# Revit family: ledtrunk_mod_l15-35w-4000-df-dali-em3-dz_549004010500
name_source: partatom
category: Leuchten
revit_build: Autodesk Revit 2016 (Build: 20190508_0715(x64)
units: mm (PartAtom-declared; Revit-internal decimal feet)

## family parameters
Basisbauteil = Fläche
Beim Laden mit Abzugskörper schneiden = Nein
Bemaßung runder Anschluss = Durchmesser verwenden
Gemeinsam genutzt = Nein
Lichtquelle = Nein
Raumberechnungspunkt = Nein
Teiletyp = Normal

## types (1)
- LEDTrunk Mod L15-35W-4000-DF-DALI-EM3-DZ (1 x LED, 5250 lm, 4000)
    Approval mark = CE, ENEC
    Beschreibung = Professional LED light line solution. Simple installation with snap-in mounting of LED modules and trunks. Integration of 3C Spots possible with 3C Track Module accessory.
    CIE Flux Codes = 41 71 90 89 99
    Color Rendering = 80
    Color Temperature = 4000
    Control Gear = Electronic ballast
    Frequency = 60 Hz
    Height = 66 mm
    Hersteller = OPPLE
    Lamp Light Flux = 5250 lm
    Lamp count = 1
    Lampe = 1 x LED
    Length = 1498 mm
    Luminous efficacy = 150 lm/W
    ModVariant = Nein
    Modell = 549004010500
    Mounting Place = Ceiling, Pole
    Mounting Type = Surface mounted, Pendant
    Number of Poles = 1
    OnlyDefault = Ja
    Power Factor = 1
    Product Name = LEDTrunk Mod L15-35W-4000-DF-DALI-EM3-DZ
    Product group = Ceiling mounted luminaire
    ProductGroupID = 3
    Protection Class = Protection class I
    Protection Degree = IP 20
    RLX_Detail_Level = 1
    RlxData = <blob elided: 50045 chars, md5=8aa27f9c>
    Scheinlast = 35 VA
    Socket = socket
    Standby Power = 0 W
    System Light Flux = 5255 lm
    System Power = 35 W
    Typenbild = web_trunk_df.jpg
    Typenkommentare = Product without accessories
    URL = http://relux.com
    VarID = ---
    Voltage = 230 V
    Voltage Range = 220-240 V
    Vorgabe-Ansicht = 1800 mm
    Weight = 0.00 kg
    Width = 78 mm  [stored 0.255906 ft]

note: [stored X ft] marks values corroborated as IEEE doubles in the binary element streams (Revit-internal decimal feet)

## geometry (parser evidence)
native form markers: Blend x4, Sweep x14
no freeform markers — native parametric forms only
